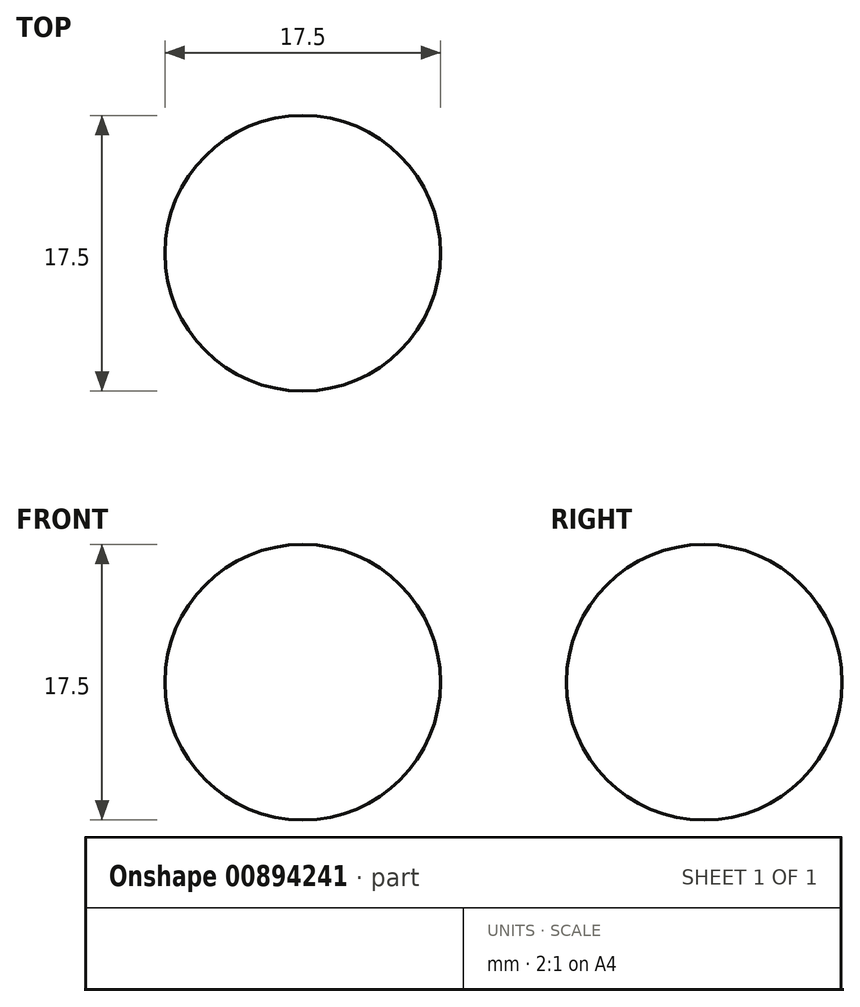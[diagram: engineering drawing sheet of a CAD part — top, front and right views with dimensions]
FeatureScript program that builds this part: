
annotation { "Feature Type Name" : "Feature", "Feature Type Description" : "" }
export const myFeature = defineFeature(function(context is Context, id is Id, definition is map)
    precondition{}
    {
        {
            var Q0;
            Q0=qCreatedBy(makeId("Front.planeOp"),FACE);
            var sketch = newSketch(context, id + "F0", { "sketchPlane" : qUnion([Q0])});
            skLineSegment(sketch, "E0", {"start": v(-8.75, 0) * mm, "end": v(8.75, 0) * mm});
            skArc(sketch, "E1", {"start": v(8.75, 0) * mm, "mid": v(0, 8.75) * mm, "end": v(-8.75, 0) * mm});
            skSolve(sketch);
        }
        {
            var Q0;
            Q0=qSketchRegion(id+"F0",true);
            var Q1;
            Q1=sQuery(id+"F0.wireOp",EDGE,"E0");
            revolve(context, id + "F1", {"surfaceOperationType" : NewSurfaceOperationType.NEW, "entities" : qUnion([Q0]), "axis" : qUnion([Q1]), "revolveType" : RevolveType.FULL});
        }
    });
